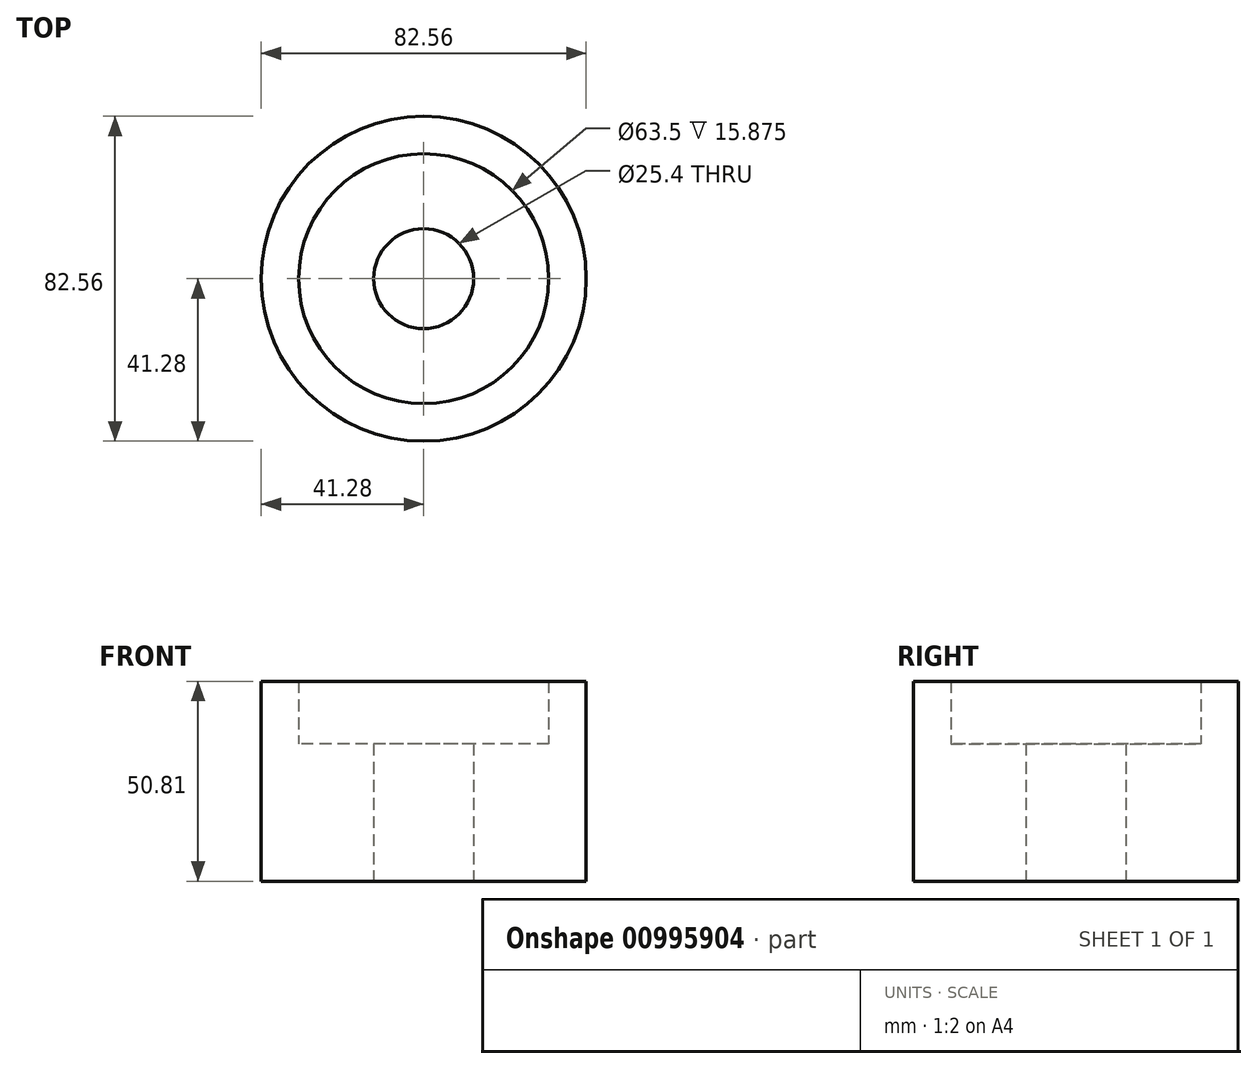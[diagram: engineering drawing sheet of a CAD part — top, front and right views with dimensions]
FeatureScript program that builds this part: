
annotation { "Feature Type Name" : "Feature", "Feature Type Description" : "" }
export const myFeature = defineFeature(function(context is Context, id is Id, definition is map)
    precondition{}
    {
        {
            var Q0;
            Q0=qCreatedBy(makeId("Top.planeOp"),FACE);
            var sketch = newSketch(context, id + "F0", { "sketchPlane" : qUnion([Q0])});
            skCircle(sketch, "E0", {"center": v(0, 0) * mm, "radius": 41.27 * mm});
            skCircle(sketch, "E1", {"center": v(0, 0) * mm, "radius": 31.75 * mm});
            skSolve(sketch);
        }
        {
            var Q0;
            Q0 = qSketchRegion(id + "F0", true);
            extrude(context, id + "F1", {"entities" : qUnion([Q0]), "depth" : 15.88 * mm, "offsetDistance" : 25.4 * mm});
        }
        {
            var Q0;
            Q0=makeQuery(id+"F0.imprint","IMPRINT",FACE,{"disambiguationData":[TD([[makeQuery(id+"F0.imprint","IMPRINT",EDGE,{"derivedFrom":sQuery(id+"F0.wireOp",EDGE,"E0")}),1.0]])]});
            var sketch = newSketch(context, id + "F2", { "sketchPlane" : qUnion([Q0])});
            skCircle(sketch, "E2", {"center": v(0, 0) * mm, "radius": 41.28 * mm});
            skSolve(sketch);
        }
        {
            var Q0;
            Q0 = qSketchRegion(id + "F2", true);
            extrude(context, id + "F3", {"entities" : qUnion([Q0]), "operationType" : NewBodyOperationType.ADD, "depth" : -34.92 * mm, "offsetDistance" : 25.4 * mm});
        }
        {
            var Q0;
            {var subQ0=sQuery(id+"F2.wireOp",EDGE,"E2");Q0=makeQuery(id+"FEZecqWQpLeFw9u_1.boolean.opBoolean","SPLIT",FACE,{"disambiguationData":[TD([makeQuery(id+"FEZecqWQpLeFw9u_1.opExtrude","SWEPT_FACE",FACE,{"disambiguationData":[OSD([sQuery(id+"FtiuXcXdib0rl5T_1.wireOp",EDGE,"UzuXPj4s-ajYj-IOT6-hmhS-j20lxE4Tv1oU.right")])]})])],"derivedFrom":makeQuery(id+"F3.opExtrude","CAP_FACE",FACE,{"disambiguationData":[OSD([subQ0])],"isStart":false})});}
            var sketch = newSketch(context, id + "F4", { "sketchPlane" : qUnion([Q0])});
            skCircle(sketch, "E3", {"center": v(0, 0) * mm, "radius": 12.7 * mm});
            skSolve(sketch);
        }
        {
            var Q0;
            Q0 = qSketchRegion(id + "F4", true);
            extrude(context, id + "F5", {"entities" : qUnion([Q0]), "operationType" : NewBodyOperationType.REMOVE, "oppositeDirection" : true, "depth" : 50.8 * mm, "offsetDistance" : 25.4 * mm});
        }
    });
